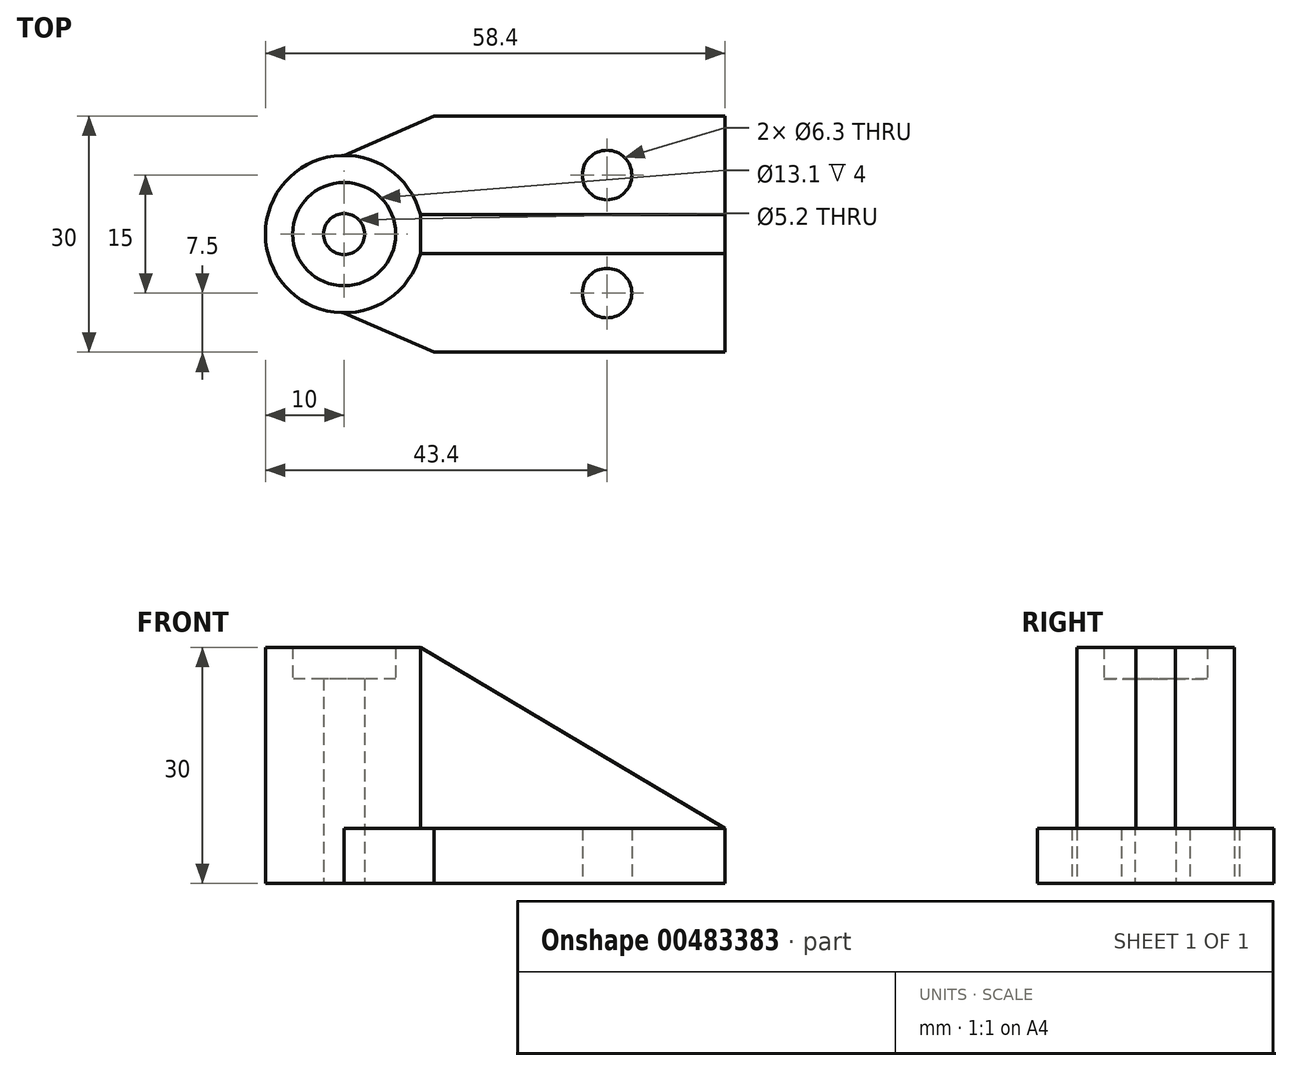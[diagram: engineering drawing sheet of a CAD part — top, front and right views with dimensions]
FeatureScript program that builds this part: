
annotation { "Feature Type Name" : "Feature", "Feature Type Description" : "" }
export const myFeature = defineFeature(function(context is Context, id is Id, definition is map)
    precondition{}
    {
        {
            var Q0;
            Q0=qCreatedBy(makeId("Top.planeOp"),FACE);
            var sketch = newSketch(context, id + "F0", { "sketchPlane" : qUnion([Q0])});
            skCircle(sketch, "E0", {"center": v(0, 0) * mm, "radius": 2.6 * mm});
            skCircle(sketch, "E1", {"center": v(0, 0) * mm, "radius": 6.55 * mm});
            skCircle(sketch, "E2", {"center": v(0, 0) * mm, "radius": 10 * mm});
            skSolve(sketch);
        }
        {
            var Q0;
            Q0=makeQuery(id+"F0.imprint","IMPRINT",FACE,{"disambiguationData":[TD([[makeQuery(id+"F0.imprint","IMPRINT",EDGE,{"derivedFrom":sQuery(id+"F0.wireOp",EDGE,"E1")}),-1.0]])]});
            extrude(context, id + "F1", {"entities" : qUnion([Q0]), "depth" : 30 * mm});
        }
        {
            var Q0;
            Q0=makeQuery(id+"F0.imprint","IMPRINT",FACE,{"disambiguationData":[TD([[makeQuery(id+"F0.imprint","IMPRINT",EDGE,{"derivedFrom":sQuery(id+"F0.wireOp",EDGE,"E0")}),-1.0]])]});
            extrude(context, id + "F2", {"entities" : qUnion([Q0]), "operationType" : NewBodyOperationType.ADD, "depth" : 26 * mm});
        }
        {
            var Q0;
            Q0=qCreatedBy(makeId("Top.planeOp"),FACE);
            var sketch = newSketch(context, id + "F3", { "sketchPlane" : qUnion([Q0])});
            skLineSegment(sketch, "E3.bottom", {"start": v(11.4, 15) * mm, "end": v(48.4, 15) * mm});
            skLineSegment(sketch, "E3.top", {"start": v(11.4, -15) * mm, "end": v(48.4, -15) * mm});
            skLineSegment(sketch, "E3.left", {"start": v(11.4, 15) * mm, "end": v(11.4, -15) * mm});
            skLineSegment(sketch, "E3.right", {"start": v(48.4, 15) * mm, "end": v(48.4, -15) * mm});
            skLineSegment(sketch, "E4", {"start": v(18.4, 15) * mm, "end": v(18.4, -15) * mm});
            skCircle(sketch, "E5", {"center": v(0, 0) * mm, "radius": 10 * mm});
            skLineSegment(sketch, "E6", {"start": v(0, 10) * mm, "end": v(11.4, 15) * mm});
            skLineSegment(sketch, "E7", {"start": v(0, -10) * mm, "end": v(11.4, -15) * mm});
            skCircle(sketch, "E8", {"center": v(0, 0) * mm, "radius": 6.65 * mm});
            skSolve(sketch);
        }
        {
            var Q0;
            Q0=makeQuery(id+"F3.imprint","IMPRINT",FACE,{"disambiguationData":[TD([[makeQuery(id+"F3.imprint","IMPRINT",EDGE,{"derivedFrom":sQuery(id+"F3.wireOp",EDGE,"E3.left")}),-1.0]])]});
            var Q1;
            {var subQ0=sQuery(id+"F3.wireOp",EDGE,"E3.left");Q1=makeQuery(id+"F3.imprint","IMPRINT",FACE,{"disambiguationData":[TD([[makeQuery(id+"F3.imprint","IMPRINT",EDGE,{"derivedFrom":subQ0}),1.0]])]});}
            var Q2;
            {var subQ0=sQuery(id+"F3.wireOp",EDGE,"E3.right");Q2=makeQuery(id+"F3.imprint","IMPRINT",FACE,{"disambiguationData":[TD([[makeQuery(id+"F3.imprint","IMPRINT",EDGE,{"derivedFrom":subQ0}),-1.0]])]});}
            extrude(context, id + "F4", {"entities" : qUnion([Q0, Q1, Q2]), "operationType" : NewBodyOperationType.ADD, "depth" : 7 * mm});
        }
        {
            var Q0;
            {var subQ0=sQuery(id+"F3.wireOp",EDGE,"E3.left");Q0=makeQuery(id+"F3.imprint","IMPRINT",FACE,{"disambiguationData":[TD([[makeQuery(id+"F3.imprint","IMPRINT",EDGE,{"derivedFrom":subQ0}),1.0]])]});}
            extrude(context, id + "F5", {"entities" : qUnion([Q0]), "operationType" : NewBodyOperationType.ADD, "oppositeDirection" : true, "depth" : 30 * mm});
        }
        {
            var Q0;
            Q0=makeQuery(id+"F4.opExtrude","CAP_FACE",FACE,{"disambiguationData":[OSD([sQuery(id+"F3.wireOp",EDGE,"E3.bottom"),sQuery(id+"F3.wireOp",EDGE,"E3.top"),sQuery(id+"F3.wireOp",EDGE,"E3.right"),sQuery(id+"F3.wireOp",EDGE,"E5"),sQuery(id+"F3.wireOp",EDGE,"E6"),sQuery(id+"F3.wireOp",EDGE,"E7")])],"isStart":false});
            var sketch = newSketch(context, id + "F6", { "sketchPlane" : qUnion([Q0])});
            skLineSegment(sketch, "E9.bottom", {"start": v(8.4, 2.5) * mm, "end": v(48.4, 2.5) * mm});
            skLineSegment(sketch, "E9.top", {"start": v(8.4, -2.5) * mm, "end": v(48.4, -2.5) * mm});
            skLineSegment(sketch, "E9.left", {"start": v(8.4, 2.5) * mm, "end": v(8.4, -2.5) * mm});
            skLineSegment(sketch, "E9.right", {"start": v(48.4, 2.5) * mm, "end": v(48.4, -2.5) * mm});
            skSolve(sketch);
        }
        {
            var Q0;
            Q0 = qSketchRegion(id + "F6", true);
            var Q1;
            Q1=makeQuery(id+"F1.opExtrude","CAP_FACE",FACE,{"disambiguationData":[OSD([sQuery(id+"F0.wireOp",EDGE,"E1"),sQuery(id+"F0.wireOp",EDGE,"E2")])],"isStart":false});
            extrude(context, id + "F7", {"entities" : qUnion([Q0]), "operationType" : NewBodyOperationType.ADD, "endBound" : BoundingType.UP_TO_SURFACE, "endBoundEntityFace" : qUnion([Q1]), "depth" : 25 * mm});
        }
        {
            var Q0;
            Q0=makeQuery(id+"F7.opExtrude","SWEPT_FACE",FACE,{"disambiguationData":[OSD([sQuery(id+"F6.wireOp",EDGE,"E9.top")])]});
            var sketch = newSketch(context, id + "F8", { "sketchPlane" : qUnion([Q0])});
            skLineSegment(sketch, "E10", {"start": v(9.68, 30) * mm, "end": v(48.4, 7) * mm});
            skLineSegment(sketch, "E11", {"start": v(48.4, 7) * mm, "end": v(48.4, 30) * mm});
            skLineSegment(sketch, "E12", {"start": v(48.4, 30) * mm, "end": v(9.68, 30) * mm});
            skSolve(sketch);
        }
        {
            var Q0;
            Q0 = qSketchRegion(id + "F8", true);
            extrude(context, id + "F9", {"entities" : qUnion([Q0]), "operationType" : NewBodyOperationType.REMOVE, "oppositeDirection" : true, "depth" : 25 * mm});
        }
        {
            var Q0;
            Q0=makeQuery(id+"F5.opExtrude","SWEPT_FACE",FACE,{"disambiguationData":[OSD([sQuery(id+"F3.wireOp",EDGE,"E4")])]});
            var sketch = newSketch(context, id + "F10", { "sketchPlane" : qUnion([Q0])});
            skCircle(sketch, "E13", {"center": v(-7.5, -15) * mm, "radius": 3.15 * mm});
            skCircle(sketch, "E14", {"center": v(7.5, -15) * mm, "radius": 3.15 * mm});
            skSolve(sketch);
        }
        {
            var Q0;
            Q0 = qSketchRegion(id + "F10", true);
            extrude(context, id + "F11", {"entities" : qUnion([Q0]), "operationType" : NewBodyOperationType.REMOVE, "oppositeDirection" : true, "depth" : 25 * mm});
        }
        {
            var Q0;
            {var subQ0=sQuery(id+"F3.wireOp",EDGE,"E3.right");Q0=makeQuery(id+"F3.imprint","IMPRINT",FACE,{"disambiguationData":[TD([[makeQuery(id+"F3.imprint","IMPRINT",EDGE,{"derivedFrom":subQ0}),-1.0]])]});}
            var sketch = newSketch(context, id + "F12", { "sketchPlane" : qUnion([Q0])});
            skCircle(sketch, "E15", {"center": v(33.4, -7.5) * mm, "radius": 3.15 * mm});
            skCircle(sketch, "E16", {"center": v(33.4, 7.5) * mm, "radius": 3.15 * mm});
            skSolve(sketch);
        }
        {
            var Q0;
            Q0 = qSketchRegion(id + "F12", true);
            extrude(context, id + "F13", {"entities" : qUnion([Q0]), "operationType" : NewBodyOperationType.REMOVE, "depth" : 25 * mm});
        }
        {
            var Q0;
            {var subQ0=sQuery(id+"F3.wireOp",EDGE,"E3.top");Q0=makeQuery(id+"F5.boolean.opBoolean","MERGE",FACE,{"derivedFrom":[makeQuery(id+"F4.opExtrude","SWEPT_FACE",FACE,{"disambiguationData":[OSD([subQ0])]}),makeQuery(id+"F5.opExtrude","SWEPT_FACE",FACE,{"disambiguationData":[OSD([subQ0])]})]});}
            var sketch = newSketch(context, id + "F14", { "sketchPlane" : qUnion([Q0])});
            skLineSegment(sketch, "E17", {"start": v(48.4, 0) * mm, "end": v(-16.94, 0) * mm});
            skLineSegment(sketch, "E18", {"start": v(-16.94, 0) * mm, "end": v(-15.38, -41.37) * mm});
            skLineSegment(sketch, "E19", {"start": v(-15.38, -41.37) * mm, "end": v(51.2, -41.37) * mm});
            skLineSegment(sketch, "E20", {"start": v(51.2, -41.37) * mm, "end": v(48.4, 0) * mm});
            skSolve(sketch);
        }
        {
            var Q0;
            Q0 = qSketchRegion(id + "F14", true);
            extrude(context, id + "F15", {"entities" : qUnion([Q0]), "operationType" : NewBodyOperationType.REMOVE, "endBound" : BoundingType.THROUGH_ALL, "oppositeDirection" : true, "depth" : 25 * mm});
        }
    });
